# Revit family: Blucher_PlumbingFixture_Domestic_TwoPartDrainWithSideInlet_150mm_Vinyl1
name_source: partatom
category: Plumbing Fixtures
revit_build: Autodesk Revit 2017 (Build: 20190508_0315(x64)
units: mm (PartAtom-declared; Revit-internal decimal feet)

## family parameters
Cut with Voids When Loaded = No
Host = Face
OmniClass Number = 23.70.50.21.24
OmniClass Title = Waste Water Drains
Part Type = Normal
Room Calculation Point = No
Round Connector Dimension = Use Diameter
Shared = No

## types (1)
- Circle
    Angle2 = 90.00°
    Assembly Code = D2030300
    AssetType = Fixed
    BIMObjectName = Blucher_PlumbingFixture_Domestic_TwoPartDrain_150mm_Vinyl
    CW Connection = No
    ChannelOutletMaxHeight = 313 mm  [stored 1.0269 ft]
    ChannelOutletMinHeight = 283 mm  [stored 0.928478 ft]
    ClassificationName = Uniclass2015
    ClassificationValue = Pr_65_52_24_24
    Color = Stainless Steel
    D = 110 mm  [stored 0.360892 ft]
    Default Elevation = 0 mm  [stored 0 ft]
    Description = Domestic Drains - Floor: Vinyl
    DocumentationCertificates = https://www.bimstore.co
    DocumentationInstallationGuide = https://www.bimstore.co
    DocumentationInstallationVideo = http://www.blucher.com
    DocumentationLiterature = https://www.bimstore.co
    DocumentationMaintenance = https://www.bimstore.co
    DocumentationTechnical = https://www.bimstore.co
    DrainProductCode = 000.000.000
    DurationUnit = Years
    ExpectedLife = 50
    F = 222 mm
    F1 = 222 mm
    FilterBasket_ 502.000.000 S = FB : 502.000.000 S
    Finish = 2B - Pickled
    Grade = AISI 304/EN 1.4301 or AISI 316L/EN 1.4404
    GratingProductCode = 610.155.421
    H = 68 mm  [stored 0.223097 ft]
    H1 = 60 mm  [stored 0.19685 ft]
    H4 = 211 mm  [stored 0.692257 ft]
    H5 = 8 mm  [stored 0.0262467 ft]
    HW Connection = No
    HeightFromLevel = 0 mm  [stored 0 ft]
    HorizontalOutletHeight = 260 mm  [stored 0.853018 ft]
    HorizontalOutletLength = 260 mm  [stored 0.853018 ft]
    IfcExportAs = IfcFlowTerminal
    IfcExportType = IfcWasteTerminalTypeEnum.FLOORWASTE
    Keynote = R10
    LowerPartDiameter = 75 mm
    LowerPartHeight = 260 mm  [stored 0.853018 ft]
    LowerPartType = LP_V_151.000 : 075 - 110
    LowerPart_111.000.075 = LP_H_111.000 : 075 - 110
    LowerPart_151.000.075 = LP_V_151.000 : 075 - 110
    LowerPart_151.000.110 = LP_V_151.000 : 110 - 110
    Manufacturer = BLÜCHER
    ManufacturerName = BLÜCHER
    Material = Available in Stainless Steel AISI 304 & Stainless Steel AISI 316L
    Model = BLÜCHER Two Part Drain With Side Inlet 150mm Circle
    ModelReference = BLÜCHER Two Part Drain With Side Inlet 150mm Circle
    NBSDescription = Drainage channels with gratings
    NBSObjectName = BLÜCHER - Drainage channels with gratings
    NBSReference = 90-05-20/422
    NominalDepth = 222 mm
    NominalLength = 222 mm
    ProductionYear = 2019
    ReferencedStandard = EN1253
    Shape = Square
    SideInletDia = 32 mm  [stored 0.104987 ft]
    SideInletType = SI : 32mm
    SideOutletLowerPartWidth = 140 mm  [stored 0.459318 ft]
    Size = 150mm(W) x 150mm(L) x 100mm(H)
    Type Comments = Two Part Drain
    TypeName = Two Part Drain
    URL = http://www.blucher.com
    UpperPartType = UP_210.300.050 : 210.300.050
    Vent Connection = No
    WarrantyDurationUnit = Years
    Waste Connection = Yes
    WaterTrap_502.050.010 = WT : 502.050.010
    _BSBibleVersion = 15
    _BimSpecGuid = 0
    _CurrentRevision = 1
    _DistributedBy = www.bimstore.co.uk

note: [stored X ft] marks values corroborated as IEEE doubles in the binary element streams (Revit-internal decimal feet)

## geometry (parser evidence)
native form markers: Blend x12, Sweep x22
no freeform markers — native parametric forms only
